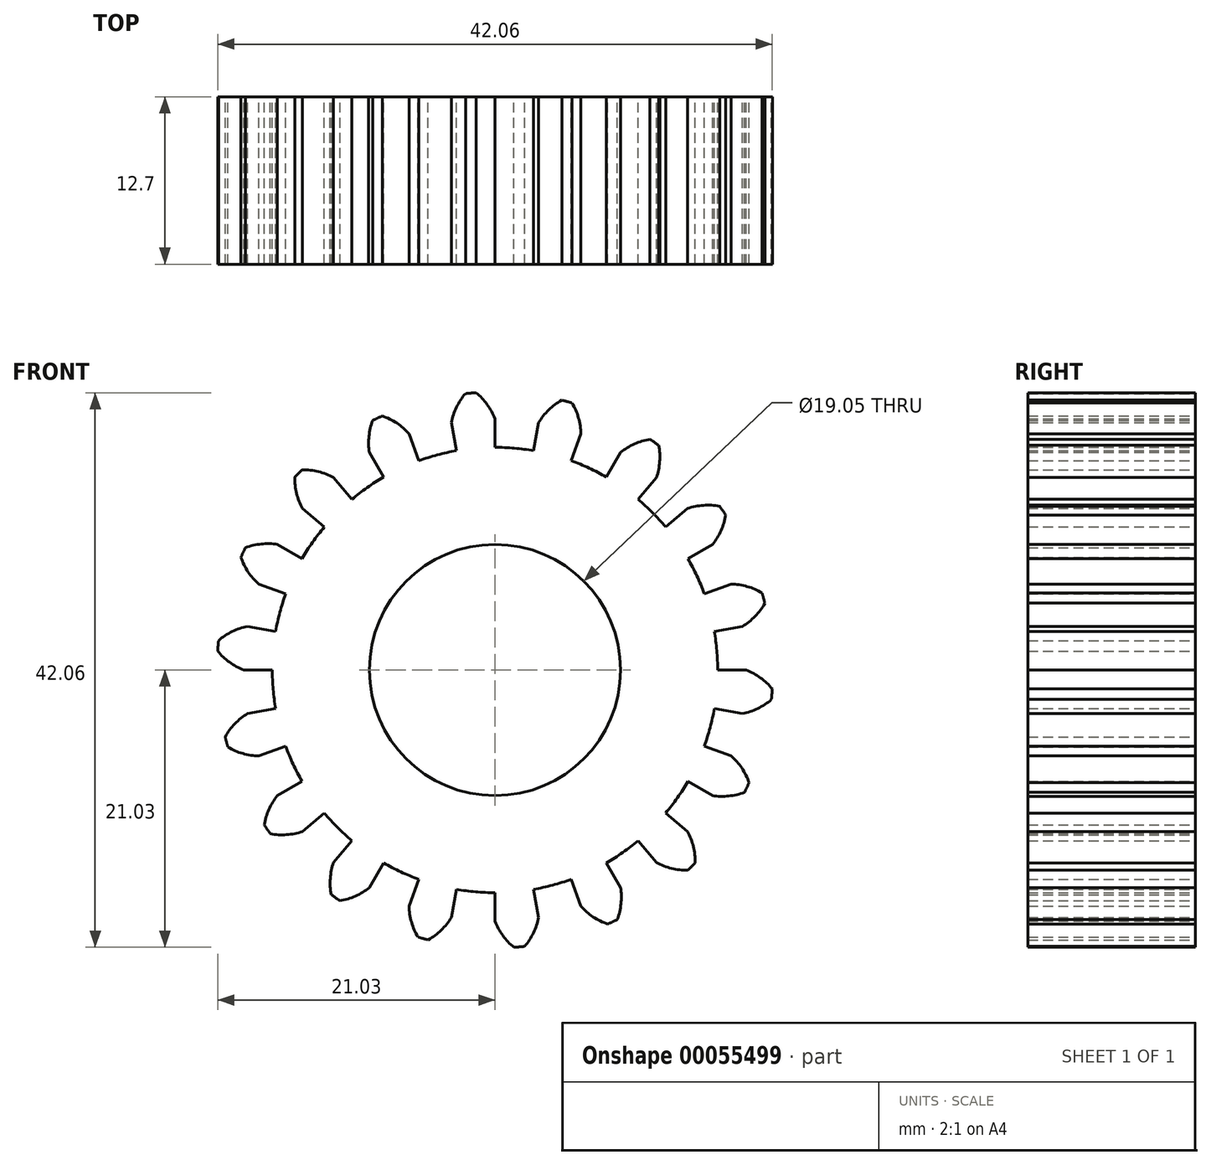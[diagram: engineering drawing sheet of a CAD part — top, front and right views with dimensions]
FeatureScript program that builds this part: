
annotation { "Feature Type Name" : "Feature", "Feature Type Description" : "" }
export const myFeature = defineFeature(function(context is Context, id is Id, definition is map)
    precondition{}
    {
        {
            var Q0;
            Q0=qCreatedBy(makeId("Front.planeOp"),FACE);
            var sketch = newSketch(context, id + "F0", { "sketchPlane" : qUnion([Q0])});
            skArc(sketch, "E0", {"start": v(-2.93, 16.63) * mm, "mid": v(-4.37, 16.32) * mm, "end": v(-5.78, 15.87) * mm});
            skArc(sketch, "E1", {"start": v(-1.44, 21.03) * mm, "mid": v(-1.64, 21.02) * mm, "end": v(-1.84, 21) * mm});
            skArc(sketch, "E2.trimOffspring", {"start": v(0, 19.05) * mm, "mid": v(-0.59, 20.14) * mm, "end": v(-1.44, 21.03) * mm});
            skLineSegment(sketch, "E3", {"start": v(-1.44, 21.03) * mm, "end": v(-1.84, 21) * mm});
            skLineSegment(sketch, "E4", {"start": v(0, 19.05) * mm, "end": v(0, 16.9) * mm});
            skArc(sketch, "E5.MirrorCS", {"start": v(-2.24, 20.96) * mm, "mid": v(-2.04, 20.98) * mm, "end": v(-1.84, 21) * mm});
            skLineSegment(sketch, "E6.MirrorCS", {"start": v(-3.3, 18.76) * mm, "end": v(-2.93, 16.63) * mm});
            skLineSegment(sketch, "E7.MirrorCS", {"start": v(-2.24, 20.96) * mm, "end": v(-1.84, 21) * mm});
            skArc(sketch, "E8.MirrorCS", {"start": v(-3.3, 18.76) * mm, "mid": v(-2.92, 19.93) * mm, "end": v(-2.24, 20.96) * mm});
            skLineSegment(sketch, "E9.trimOffspring", {"start": v(-1.84, 21) * mm, "end": v(-1.84, 21) * mm, "construction": true});
            skArc(sketch, "E10.1.0", {"start": v(3.3, 18.76) * mm, "mid": v(4.08, 19.73) * mm, "end": v(5.07, 20.46) * mm});
            skLineSegment(sketch, "E10.1.1", {"start": v(3.3, 18.76) * mm, "end": v(2.93, 16.63) * mm});
            skLineSegment(sketch, "E10.1.2", {"start": v(6.52, 17.9) * mm, "end": v(5.78, 15.87) * mm});
            skArc(sketch, "E10.1.3", {"start": v(6.52, 17.9) * mm, "mid": v(6.33, 19.12) * mm, "end": v(5.84, 20.26) * mm});
            skLineSegment(sketch, "E10.1.4", {"start": v(5.84, 20.26) * mm, "end": v(5.46, 20.37) * mm});
            skLineSegment(sketch, "E10.1.5", {"start": v(5.07, 20.46) * mm, "end": v(5.46, 20.37) * mm});
            skArc(sketch, "E10.1.6", {"start": v(5.07, 20.46) * mm, "mid": v(5.26, 20.41) * mm, "end": v(5.46, 20.36) * mm});
            skArc(sketch, "E10.1.7", {"start": v(5.84, 20.26) * mm, "mid": v(5.65, 20.31) * mm, "end": v(5.46, 20.36) * mm});
            skArc(sketch, "E10.2.0", {"start": v(9.53, 16.5) * mm, "mid": v(10.58, 17.14) * mm, "end": v(11.76, 17.5) * mm});
            skLineSegment(sketch, "E10.2.1", {"start": v(9.53, 16.5) * mm, "end": v(8.45, 14.63) * mm});
            skLineSegment(sketch, "E10.2.2", {"start": v(12.25, 14.6) * mm, "end": v(10.86, 12.94) * mm});
            skArc(sketch, "E10.2.3", {"start": v(12.25, 14.6) * mm, "mid": v(12.5, 15.8) * mm, "end": v(12.42, 17.04) * mm});
            skLineSegment(sketch, "E10.2.4", {"start": v(12.42, 17.04) * mm, "end": v(12.1, 17.27) * mm});
            skLineSegment(sketch, "E10.2.5", {"start": v(11.76, 17.5) * mm, "end": v(12.1, 17.27) * mm});
            skArc(sketch, "E10.2.6", {"start": v(11.76, 17.5) * mm, "mid": v(11.93, 17.38) * mm, "end": v(12.1, 17.27) * mm});
            skArc(sketch, "E10.2.7", {"start": v(12.42, 17.04) * mm, "mid": v(12.26, 17.15) * mm, "end": v(12.1, 17.27) * mm});
            skArc(sketch, "E10.3.0", {"start": v(14.6, 12.25) * mm, "mid": v(15.8, 12.5) * mm, "end": v(17.04, 12.42) * mm});
            skLineSegment(sketch, "E10.3.1", {"start": v(14.6, 12.25) * mm, "end": v(12.94, 10.86) * mm});
            skLineSegment(sketch, "E10.3.2", {"start": v(16.5, 9.52) * mm, "end": v(14.63, 8.45) * mm});
            skArc(sketch, "E10.3.3", {"start": v(16.5, 9.52) * mm, "mid": v(17.14, 10.58) * mm, "end": v(17.5, 11.76) * mm});
            skLineSegment(sketch, "E10.3.4", {"start": v(17.5, 11.76) * mm, "end": v(17.27, 12.1) * mm});
            skLineSegment(sketch, "E10.3.5", {"start": v(17.04, 12.42) * mm, "end": v(17.27, 12.1) * mm});
            skArc(sketch, "E10.3.6", {"start": v(17.04, 12.42) * mm, "mid": v(17.15, 12.26) * mm, "end": v(17.27, 12.1) * mm});
            skArc(sketch, "E10.3.7", {"start": v(17.5, 11.76) * mm, "mid": v(17.38, 11.93) * mm, "end": v(17.27, 12.1) * mm});
            skArc(sketch, "E10.4.0", {"start": v(17.9, 6.52) * mm, "mid": v(19.12, 6.33) * mm, "end": v(20.26, 5.84) * mm});
            skLineSegment(sketch, "E10.4.1", {"start": v(17.9, 6.52) * mm, "end": v(15.87, 5.78) * mm});
            skLineSegment(sketch, "E10.4.2", {"start": v(18.76, 3.3) * mm, "end": v(16.63, 2.93) * mm});
            skArc(sketch, "E10.4.3", {"start": v(18.76, 3.3) * mm, "mid": v(19.73, 4.08) * mm, "end": v(20.46, 5.07) * mm});
            skLineSegment(sketch, "E10.4.4", {"start": v(20.46, 5.07) * mm, "end": v(20.37, 5.46) * mm});
            skLineSegment(sketch, "E10.4.5", {"start": v(20.26, 5.84) * mm, "end": v(20.37, 5.46) * mm});
            skArc(sketch, "E10.4.6", {"start": v(20.26, 5.84) * mm, "mid": v(20.31, 5.65) * mm, "end": v(20.36, 5.46) * mm});
            skArc(sketch, "E10.4.7", {"start": v(20.46, 5.07) * mm, "mid": v(20.41, 5.26) * mm, "end": v(20.36, 5.46) * mm});
            skArc(sketch, "E10.5.0", {"start": v(19.05, 0) * mm, "mid": v(20.14, -0.59) * mm, "end": v(21.03, -1.44) * mm});
            skLineSegment(sketch, "E10.5.1", {"start": v(19.05, 0) * mm, "end": v(16.9, 0) * mm});
            skLineSegment(sketch, "E10.5.2", {"start": v(18.76, -3.3) * mm, "end": v(16.63, -2.93) * mm});
            skArc(sketch, "E10.5.3", {"start": v(18.76, -3.3) * mm, "mid": v(19.93, -2.92) * mm, "end": v(20.96, -2.24) * mm});
            skLineSegment(sketch, "E10.5.4", {"start": v(20.96, -2.24) * mm, "end": v(21, -1.84) * mm});
            skLineSegment(sketch, "E10.5.5", {"start": v(21.03, -1.44) * mm, "end": v(21, -1.84) * mm});
            skArc(sketch, "E10.5.6", {"start": v(21.03, -1.44) * mm, "mid": v(21.02, -1.64) * mm, "end": v(21, -1.84) * mm});
            skArc(sketch, "E10.5.7", {"start": v(20.96, -2.24) * mm, "mid": v(20.98, -2.04) * mm, "end": v(21, -1.84) * mm});
            skArc(sketch, "E10.6.0", {"start": v(17.9, -6.52) * mm, "mid": v(18.72, -7.44) * mm, "end": v(19.27, -8.54) * mm});
            skLineSegment(sketch, "E10.6.1", {"start": v(17.9, -6.52) * mm, "end": v(15.87, -5.78) * mm});
            skLineSegment(sketch, "E10.6.2", {"start": v(16.5, -9.53) * mm, "end": v(14.63, -8.45) * mm});
            skArc(sketch, "E10.6.3", {"start": v(16.5, -9.53) * mm, "mid": v(17.73, -9.56) * mm, "end": v(18.93, -9.27) * mm});
            skLineSegment(sketch, "E10.6.4", {"start": v(18.93, -9.27) * mm, "end": v(19.11, -8.91) * mm});
            skLineSegment(sketch, "E10.6.5", {"start": v(19.27, -8.54) * mm, "end": v(19.11, -8.91) * mm});
            skArc(sketch, "E10.6.6", {"start": v(19.27, -8.54) * mm, "mid": v(19.2, -8.73) * mm, "end": v(19.1, -8.9) * mm});
            skArc(sketch, "E10.6.7", {"start": v(18.93, -9.27) * mm, "mid": v(19.02, -9.1) * mm, "end": v(19.1, -8.9) * mm});
            skArc(sketch, "E10.7.0", {"start": v(14.6, -12.25) * mm, "mid": v(15.05, -13.4) * mm, "end": v(15.19, -14.62) * mm});
            skLineSegment(sketch, "E10.7.1", {"start": v(14.6, -12.25) * mm, "end": v(12.94, -10.86) * mm});
            skLineSegment(sketch, "E10.7.2", {"start": v(12.25, -14.6) * mm, "end": v(10.86, -12.94) * mm});
            skArc(sketch, "E10.7.3", {"start": v(12.25, -14.6) * mm, "mid": v(13.4, -15.05) * mm, "end": v(14.62, -15.19) * mm});
            skLineSegment(sketch, "E10.7.4", {"start": v(14.62, -15.19) * mm, "end": v(14.9, -14.9) * mm});
            skLineSegment(sketch, "E10.7.5", {"start": v(15.19, -14.62) * mm, "end": v(14.9, -14.9) * mm});
            skArc(sketch, "E10.7.6", {"start": v(15.19, -14.62) * mm, "mid": v(15.05, -14.76) * mm, "end": v(14.9, -14.9) * mm});
            skArc(sketch, "E10.7.7", {"start": v(14.62, -15.19) * mm, "mid": v(14.76, -15.05) * mm, "end": v(14.9, -14.9) * mm});
            skArc(sketch, "E10.8.0", {"start": v(9.52, -16.5) * mm, "mid": v(9.56, -17.73) * mm, "end": v(9.27, -18.93) * mm});
            skLineSegment(sketch, "E10.8.1", {"start": v(9.52, -16.5) * mm, "end": v(8.45, -14.63) * mm});
            skLineSegment(sketch, "E10.8.2", {"start": v(6.52, -17.9) * mm, "end": v(5.78, -15.87) * mm});
            skArc(sketch, "E10.8.3", {"start": v(6.52, -17.9) * mm, "mid": v(7.44, -18.72) * mm, "end": v(8.54, -19.27) * mm});
            skLineSegment(sketch, "E10.8.4", {"start": v(8.54, -19.27) * mm, "end": v(8.91, -19.11) * mm});
            skLineSegment(sketch, "E10.8.5", {"start": v(9.27, -18.93) * mm, "end": v(8.91, -19.11) * mm});
            skArc(sketch, "E10.8.6", {"start": v(9.27, -18.93) * mm, "mid": v(9.1, -19.02) * mm, "end": v(8.9, -19.1) * mm});
            skArc(sketch, "E10.8.7", {"start": v(8.54, -19.27) * mm, "mid": v(8.73, -19.2) * mm, "end": v(8.9, -19.1) * mm});
            skArc(sketch, "E10.9.0", {"start": v(3.3, -18.76) * mm, "mid": v(2.92, -19.93) * mm, "end": v(2.24, -20.96) * mm});
            skLineSegment(sketch, "E10.9.1", {"start": v(3.3, -18.76) * mm, "end": v(2.93, -16.63) * mm});
            skLineSegment(sketch, "E10.9.2", {"start": v(0, -19.05) * mm, "end": v(0, -16.9) * mm});
            skArc(sketch, "E10.9.3", {"start": v(0, -19.05) * mm, "mid": v(0.59, -20.14) * mm, "end": v(1.44, -21.03) * mm});
            skLineSegment(sketch, "E10.9.4", {"start": v(1.44, -21.03) * mm, "end": v(1.84, -21) * mm});
            skLineSegment(sketch, "E10.9.5", {"start": v(2.24, -20.96) * mm, "end": v(1.84, -21) * mm});
            skArc(sketch, "E10.9.6", {"start": v(2.24, -20.96) * mm, "mid": v(2.04, -20.98) * mm, "end": v(1.84, -21) * mm});
            skArc(sketch, "E10.9.7", {"start": v(1.44, -21.03) * mm, "mid": v(1.64, -21.02) * mm, "end": v(1.84, -21) * mm});
            skArc(sketch, "E10.10.0", {"start": v(-3.3, -18.76) * mm, "mid": v(-4.08, -19.73) * mm, "end": v(-5.07, -20.46) * mm});
            skLineSegment(sketch, "E10.10.1", {"start": v(-3.3, -18.76) * mm, "end": v(-2.93, -16.63) * mm});
            skLineSegment(sketch, "E10.10.2", {"start": v(-6.52, -17.9) * mm, "end": v(-5.78, -15.87) * mm});
            skArc(sketch, "E10.10.3", {"start": v(-6.52, -17.9) * mm, "mid": v(-6.33, -19.12) * mm, "end": v(-5.84, -20.26) * mm});
            skLineSegment(sketch, "E10.10.4", {"start": v(-5.84, -20.26) * mm, "end": v(-5.46, -20.37) * mm});
            skLineSegment(sketch, "E10.10.5", {"start": v(-5.07, -20.46) * mm, "end": v(-5.46, -20.37) * mm});
            skArc(sketch, "E10.10.6", {"start": v(-5.07, -20.46) * mm, "mid": v(-5.26, -20.41) * mm, "end": v(-5.46, -20.36) * mm});
            skArc(sketch, "E10.10.7", {"start": v(-5.84, -20.26) * mm, "mid": v(-5.65, -20.31) * mm, "end": v(-5.46, -20.36) * mm});
            skArc(sketch, "E10.11.0", {"start": v(-9.53, -16.5) * mm, "mid": v(-10.58, -17.14) * mm, "end": v(-11.76, -17.5) * mm});
            skLineSegment(sketch, "E10.11.1", {"start": v(-9.53, -16.5) * mm, "end": v(-8.45, -14.63) * mm});
            skLineSegment(sketch, "E10.11.2", {"start": v(-12.25, -14.6) * mm, "end": v(-10.86, -12.94) * mm});
            skArc(sketch, "E10.11.3", {"start": v(-12.25, -14.6) * mm, "mid": v(-12.5, -15.8) * mm, "end": v(-12.42, -17.04) * mm});
            skLineSegment(sketch, "E10.11.4", {"start": v(-12.42, -17.04) * mm, "end": v(-12.1, -17.27) * mm});
            skLineSegment(sketch, "E10.11.5", {"start": v(-11.76, -17.5) * mm, "end": v(-12.1, -17.27) * mm});
            skArc(sketch, "E10.11.6", {"start": v(-11.76, -17.5) * mm, "mid": v(-11.93, -17.38) * mm, "end": v(-12.1, -17.27) * mm});
            skArc(sketch, "E10.11.7", {"start": v(-12.42, -17.04) * mm, "mid": v(-12.26, -17.15) * mm, "end": v(-12.1, -17.27) * mm});
            skArc(sketch, "E10.12.0", {"start": v(-14.6, -12.25) * mm, "mid": v(-15.8, -12.5) * mm, "end": v(-17.04, -12.42) * mm});
            skLineSegment(sketch, "E10.12.1", {"start": v(-14.6, -12.25) * mm, "end": v(-12.94, -10.86) * mm});
            skLineSegment(sketch, "E10.12.2", {"start": v(-16.5, -9.52) * mm, "end": v(-14.63, -8.45) * mm});
            skArc(sketch, "E10.12.3", {"start": v(-16.5, -9.52) * mm, "mid": v(-17.14, -10.58) * mm, "end": v(-17.5, -11.76) * mm});
            skLineSegment(sketch, "E10.12.4", {"start": v(-17.5, -11.76) * mm, "end": v(-17.27, -12.1) * mm});
            skLineSegment(sketch, "E10.12.5", {"start": v(-17.04, -12.42) * mm, "end": v(-17.27, -12.1) * mm});
            skArc(sketch, "E10.12.6", {"start": v(-17.04, -12.42) * mm, "mid": v(-17.15, -12.26) * mm, "end": v(-17.27, -12.1) * mm});
            skArc(sketch, "E10.12.7", {"start": v(-17.5, -11.76) * mm, "mid": v(-17.38, -11.93) * mm, "end": v(-17.27, -12.1) * mm});
            skArc(sketch, "E10.13.0", {"start": v(-17.9, -6.52) * mm, "mid": v(-19.12, -6.33) * mm, "end": v(-20.26, -5.84) * mm});
            skLineSegment(sketch, "E10.13.1", {"start": v(-17.9, -6.52) * mm, "end": v(-15.87, -5.78) * mm});
            skLineSegment(sketch, "E10.13.2", {"start": v(-18.76, -3.3) * mm, "end": v(-16.63, -2.93) * mm});
            skArc(sketch, "E10.13.3", {"start": v(-18.76, -3.3) * mm, "mid": v(-19.73, -4.08) * mm, "end": v(-20.46, -5.07) * mm});
            skLineSegment(sketch, "E10.13.4", {"start": v(-20.46, -5.07) * mm, "end": v(-20.37, -5.46) * mm});
            skLineSegment(sketch, "E10.13.5", {"start": v(-20.26, -5.84) * mm, "end": v(-20.37, -5.46) * mm});
            skArc(sketch, "E10.13.6", {"start": v(-20.26, -5.84) * mm, "mid": v(-20.31, -5.65) * mm, "end": v(-20.36, -5.46) * mm});
            skArc(sketch, "E10.13.7", {"start": v(-20.46, -5.07) * mm, "mid": v(-20.41, -5.26) * mm, "end": v(-20.36, -5.46) * mm});
            skArc(sketch, "E10.14.0", {"start": v(-19.05, 0) * mm, "mid": v(-20.14, 0.59) * mm, "end": v(-21.03, 1.44) * mm});
            skLineSegment(sketch, "E10.14.1", {"start": v(-19.05, 0) * mm, "end": v(-16.9, 0) * mm});
            skLineSegment(sketch, "E10.14.2", {"start": v(-18.76, 3.3) * mm, "end": v(-16.63, 2.93) * mm});
            skArc(sketch, "E10.14.3", {"start": v(-18.76, 3.3) * mm, "mid": v(-19.93, 2.92) * mm, "end": v(-20.96, 2.24) * mm});
            skLineSegment(sketch, "E10.14.4", {"start": v(-20.96, 2.24) * mm, "end": v(-21, 1.84) * mm});
            skLineSegment(sketch, "E10.14.5", {"start": v(-21.03, 1.44) * mm, "end": v(-21, 1.84) * mm});
            skArc(sketch, "E10.14.6", {"start": v(-21.03, 1.44) * mm, "mid": v(-21.02, 1.64) * mm, "end": v(-21, 1.84) * mm});
            skArc(sketch, "E10.14.7", {"start": v(-20.96, 2.24) * mm, "mid": v(-20.98, 2.04) * mm, "end": v(-21, 1.84) * mm});
            skArc(sketch, "E10.15.0", {"start": v(-17.9, 6.52) * mm, "mid": v(-18.72, 7.44) * mm, "end": v(-19.27, 8.54) * mm});
            skLineSegment(sketch, "E10.15.1", {"start": v(-17.9, 6.52) * mm, "end": v(-15.87, 5.78) * mm});
            skLineSegment(sketch, "E10.15.2", {"start": v(-16.5, 9.53) * mm, "end": v(-14.63, 8.45) * mm});
            skArc(sketch, "E10.15.3", {"start": v(-16.5, 9.53) * mm, "mid": v(-17.73, 9.56) * mm, "end": v(-18.93, 9.27) * mm});
            skLineSegment(sketch, "E10.15.4", {"start": v(-18.93, 9.27) * mm, "end": v(-19.11, 8.91) * mm});
            skLineSegment(sketch, "E10.15.5", {"start": v(-19.27, 8.54) * mm, "end": v(-19.11, 8.91) * mm});
            skArc(sketch, "E10.15.6", {"start": v(-19.27, 8.54) * mm, "mid": v(-19.2, 8.73) * mm, "end": v(-19.1, 8.9) * mm});
            skArc(sketch, "E10.15.7", {"start": v(-18.93, 9.27) * mm, "mid": v(-19.02, 9.1) * mm, "end": v(-19.1, 8.9) * mm});
            skArc(sketch, "E10.16.0", {"start": v(-14.6, 12.25) * mm, "mid": v(-15.05, 13.4) * mm, "end": v(-15.19, 14.62) * mm});
            skLineSegment(sketch, "E10.16.1", {"start": v(-14.6, 12.25) * mm, "end": v(-12.94, 10.86) * mm});
            skLineSegment(sketch, "E10.16.2", {"start": v(-12.25, 14.6) * mm, "end": v(-10.86, 12.94) * mm});
            skArc(sketch, "E10.16.3", {"start": v(-12.25, 14.6) * mm, "mid": v(-13.4, 15.05) * mm, "end": v(-14.62, 15.19) * mm});
            skLineSegment(sketch, "E10.16.4", {"start": v(-14.62, 15.19) * mm, "end": v(-14.9, 14.9) * mm});
            skLineSegment(sketch, "E10.16.5", {"start": v(-15.19, 14.62) * mm, "end": v(-14.9, 14.9) * mm});
            skArc(sketch, "E10.16.6", {"start": v(-15.19, 14.62) * mm, "mid": v(-15.05, 14.76) * mm, "end": v(-14.9, 14.9) * mm});
            skArc(sketch, "E10.16.7", {"start": v(-14.62, 15.19) * mm, "mid": v(-14.76, 15.05) * mm, "end": v(-14.9, 14.9) * mm});
            skArc(sketch, "E10.17.0", {"start": v(-9.52, 16.5) * mm, "mid": v(-9.56, 17.73) * mm, "end": v(-9.27, 18.93) * mm});
            skLineSegment(sketch, "E10.17.1", {"start": v(-9.52, 16.5) * mm, "end": v(-8.45, 14.63) * mm});
            skLineSegment(sketch, "E10.17.2", {"start": v(-6.52, 17.9) * mm, "end": v(-5.78, 15.87) * mm});
            skArc(sketch, "E10.17.3", {"start": v(-6.52, 17.9) * mm, "mid": v(-7.44, 18.72) * mm, "end": v(-8.54, 19.27) * mm});
            skLineSegment(sketch, "E10.17.4", {"start": v(-8.54, 19.27) * mm, "end": v(-8.91, 19.11) * mm});
            skLineSegment(sketch, "E10.17.5", {"start": v(-9.27, 18.93) * mm, "end": v(-8.91, 19.11) * mm});
            skArc(sketch, "E10.17.6", {"start": v(-9.27, 18.93) * mm, "mid": v(-9.1, 19.02) * mm, "end": v(-8.9, 19.1) * mm});
            skArc(sketch, "E10.17.7", {"start": v(-8.54, 19.27) * mm, "mid": v(-8.73, 19.2) * mm, "end": v(-8.9, 19.1) * mm});
            skLineSegment(sketch, "E10.anchor1", {"start": v(-2.93, 16.63) * mm, "end": v(-3.3, 18.76) * mm, "construction": true});
            skLineSegment(sketch, "E10.anchor2", {"start": v(-8.45, 14.63) * mm, "end": v(-9.52, 16.5) * mm, "construction": true});
            skArc(sketch, "E11.trimOffspring", {"start": v(-8.45, 14.63) * mm, "mid": v(-9.69, 13.84) * mm, "end": v(-10.86, 12.94) * mm});
            skArc(sketch, "E12.trimOffspring", {"start": v(-12.94, 10.86) * mm, "mid": v(-13.84, 9.69) * mm, "end": v(-14.63, 8.45) * mm});
            skArc(sketch, "E13.trimOffspring", {"start": v(-15.87, 5.78) * mm, "mid": v(-16.32, 4.37) * mm, "end": v(-16.63, 2.93) * mm});
            skArc(sketch, "E14.trimOffspring", {"start": v(2.93, 16.63) * mm, "mid": v(1.47, 16.83) * mm, "end": v(0, 16.9) * mm});
            skArc(sketch, "E15.trimOffspring", {"start": v(8.45, 14.63) * mm, "mid": v(7.14, 15.3) * mm, "end": v(5.78, 15.87) * mm});
            skArc(sketch, "E16.trimOffspring", {"start": v(12.94, 10.86) * mm, "mid": v(11.94, 11.94) * mm, "end": v(10.86, 12.94) * mm});
            skArc(sketch, "E17.trimOffspring", {"start": v(15.87, 5.78) * mm, "mid": v(15.3, 7.14) * mm, "end": v(14.63, 8.45) * mm});
            skArc(sketch, "E18.trimOffspring", {"start": v(-16.9, 0) * mm, "mid": v(-16.83, -1.47) * mm, "end": v(-16.63, -2.93) * mm});
            skArc(sketch, "E19.trimOffspring", {"start": v(-15.87, -5.78) * mm, "mid": v(-15.3, -7.14) * mm, "end": v(-14.63, -8.45) * mm});
            skArc(sketch, "E20.trimOffspring", {"start": v(-12.94, -10.86) * mm, "mid": v(-11.94, -11.94) * mm, "end": v(-10.86, -12.94) * mm});
            skArc(sketch, "E21.trimOffspring", {"start": v(-8.45, -14.63) * mm, "mid": v(-7.14, -15.3) * mm, "end": v(-5.78, -15.87) * mm});
            skArc(sketch, "E22.trimOffspring", {"start": v(-2.93, -16.63) * mm, "mid": v(-1.47, -16.83) * mm, "end": v(0, -16.9) * mm});
            skArc(sketch, "E23.trimOffspring", {"start": v(2.93, -16.63) * mm, "mid": v(4.37, -16.32) * mm, "end": v(5.78, -15.87) * mm});
            skArc(sketch, "E24.trimOffspring", {"start": v(8.45, -14.63) * mm, "mid": v(9.69, -13.84) * mm, "end": v(10.86, -12.94) * mm});
            skArc(sketch, "E25.trimOffspring", {"start": v(12.94, -10.86) * mm, "mid": v(13.84, -9.69) * mm, "end": v(14.63, -8.45) * mm});
            skArc(sketch, "E26.trimOffspring", {"start": v(15.87, -5.78) * mm, "mid": v(16.32, -4.37) * mm, "end": v(16.63, -2.93) * mm});
            skArc(sketch, "E27.trimOffspring", {"start": v(16.9, 0) * mm, "mid": v(16.83, 1.47) * mm, "end": v(16.63, 2.93) * mm});
            skCircle(sketch, "E28", {"center": v(0, 0) * mm, "radius": 9.53 * mm});
            skSolve(sketch);
        }
        {
            var Q0;
            Q0=makeQuery(id+"F0.imprint","IMPRINT",FACE,{"disambiguationData":[TD([[makeQuery(id+"F0.imprint","IMPRINT",EDGE,{"derivedFrom":sQuery(id+"F0.wireOp",EDGE,"E0")}),1.0]])]});
            extrude(context, id + "F1", {"entities" : qUnion([Q0]), "depth" : 12.7 * mm});
        }
    });
